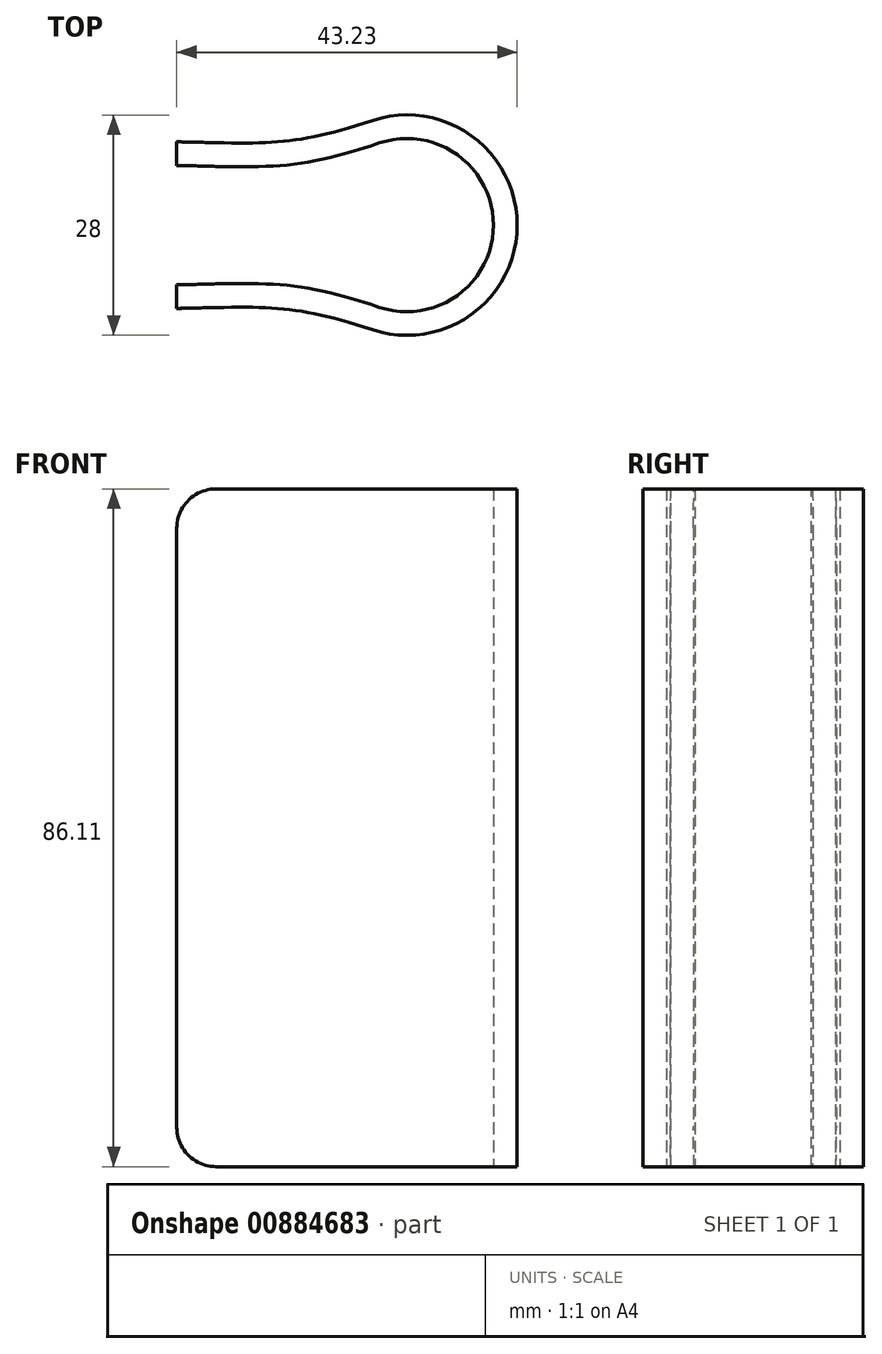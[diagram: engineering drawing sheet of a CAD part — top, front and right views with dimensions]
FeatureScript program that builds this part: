
annotation { "Feature Type Name" : "Feature", "Feature Type Description" : "" }
export const myFeature = defineFeature(function(context is Context, id is Id, definition is map)
    precondition{}
    {
        {
            var Q0;
            Q0=qCreatedBy(makeId("Top.planeOp"),FACE);
            var sketch = newSketch(context, id + "F0", { "sketchPlane" : qUnion([Q0])});
            skArc(sketch, "E0", {"start": v(-4.38, -13.3) * mm, "mid": v(14, 0) * mm, "end": v(-4.38, 13.3) * mm});
            skLineSegment(sketch, "E1", {"start": v(-29.23, 7.58) * mm, "end": v(-29.23, 10.59) * mm});
            skFitSpline(sketch, "E2", {"points": [v(-29.23, 10.59) * mm, v(-4.38, 13.3) * mm], "startDerivative": vector(35.33, -0.76) * mm, "endDerivative": vector(30.03, 9.9) * mm});
            skFitSpline(sketch, "E3.MirrorCS", {"points": [v(-29.23, -10.59) * mm, v(-4.38, -13.3) * mm], "startDerivative": vector(35.33, 0.76) * mm, "endDerivative": vector(30.03, -9.9) * mm});
            skLineSegment(sketch, "E4.MirrorCS", {"start": v(-29.23, -7.58) * mm, "end": v(-29.23, -10.59) * mm});
            skFitSpline(sketch, "E5.0", {"points": [v(-29.3, -7.59) * mm, v(-26.36, -7.52) * mm, v(-22.75, -7.42) * mm, v(-18.72, -7.44) * mm, v(-15.88, -7.59) * mm, v(-13.09, -7.92) * mm, v(-10.2, -8.48) * mm, v(-7.08, -9.3) * mm, v(-4.72, -10.03) * mm, v(-3.44, -10.45) * mm]});
            skArc(sketch, "E5.1", {"start": v(-3.44, -10.45) * mm, "mid": v(11, 0) * mm, "end": v(-3.44, 10.45) * mm});
            skFitSpline(sketch, "E5.2", {"points": [v(-29.3, 7.59) * mm, v(-26.36, 7.52) * mm, v(-22.75, 7.42) * mm, v(-18.72, 7.44) * mm, v(-15.88, 7.59) * mm, v(-13.09, 7.92) * mm, v(-10.2, 8.48) * mm, v(-7.08, 9.3) * mm, v(-4.72, 10.03) * mm, v(-3.44, 10.45) * mm]});
            skPoint(sketch, "E6.orphan", {"position": v(-29.23, 0) * mm});
            skSolve(sketch);
        }
        {
            var Q0;
            Q0=makeQuery(id+"F0.imprint","IMPRINT",FACE,{"disambiguationData":[TD([[makeQuery(id+"F0.imprint","IMPRINT",EDGE,{"derivedFrom":sQuery(id+"F0.wireOp",EDGE,"E0")}),1.0]])]});
            extrude(context, id + "F1", {"entities" : qUnion([Q0]), "depth" : 86.11 * mm, "offsetDistance" : 25 * mm});
        }
        {
            var Q0;
            Q0=makeQuery(id+"F1.opExtrude","CAP_EDGE",EDGE,{"disambiguationData":[OSD([sQuery(id+"F0.wireOp",EDGE,"E4.MirrorCS")])],"isStart":true});
            fillet(context, id + "F2", {"entities" : qUnion([Q0]), "radius" : 5 * mm, "tangentPropagation" : true, "allowEdgeOverflow" : false});
        }
        {
            var Q0;
            Q0=makeQuery(id+"F1.opExtrude","CAP_EDGE",EDGE,{"disambiguationData":[OSD([sQuery(id+"F0.wireOp",EDGE,"E1")])],"isStart":true});
            fillet(context, id + "F3", {"entities" : qUnion([Q0]), "radius" : 5 * mm, "tangentPropagation" : true, "allowEdgeOverflow" : false});
        }
        {
            var Q0;
            Q0=makeQuery(id+"F1.opExtrude","CAP_EDGE",EDGE,{"disambiguationData":[OSD([sQuery(id+"F0.wireOp",EDGE,"E4.MirrorCS")])],"isStart":false});
            var Q1;
            Q1=makeQuery(id+"F1.opExtrude","CAP_EDGE",EDGE,{"disambiguationData":[OSD([sQuery(id+"F0.wireOp",EDGE,"E1")])],"isStart":false});
            fillet(context, id + "F4", {"entities" : qUnion([Q0, Q1]), "radius" : 5 * mm, "tangentPropagation" : true, "allowEdgeOverflow" : false});
        }
    });
